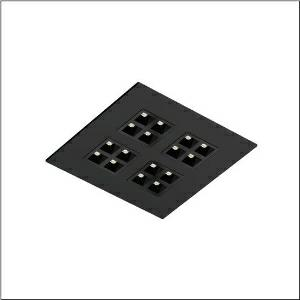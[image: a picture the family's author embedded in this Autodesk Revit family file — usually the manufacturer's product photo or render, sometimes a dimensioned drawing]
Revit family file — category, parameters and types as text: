
# Revit family: silica_31_square_51my6lmu34ba
name_source: partatom
category: Lighting Fixtures
units: mm (PartAtom-declared; Revit-internal decimal feet)

## family parameters
Cut with Voids When Loaded = No
Host = Face
Light Source = No
Part Type = Normal
Room Calculation Point = No
Round Connector Dimension = Use Diameter
Shared = No

## types (1)
- --- (1 x LED, 6250 lm, 39 W, 3000K)
    Apparent Load = 39 VA
    CIE Flux Codes = 82 100 100 100 100
    Color Rendering = 80
    Color Temperature = 3000K
    Default Elevation = 1800 mm
    Description = Silica 31 Square, office luminaire, primary light control with lens, of PMMA, primary anti-glare with reflector, of PC, black, light emission: direct distribution, primary light characteristic: symmetric, installation type: lay-in mounting, LED, rated luminous flux: 4.600lm, luminous efficacy: 166lm/W, light colour: 830, colour temperature: 3000K, control gear: ON/OFF Multilumen, with terminal, 3-pole, mains connection: 220..240V, AC, 50/60Hz, rated input power: 27.7W, luminaire housing, of sheet steel, coated, jet black (RAL 9005), module: M625, length: 620mm, width: 620mm, height: 43mm, protection rating (complete): IP20, insulation class (complete): insulation class II (safety insulation), certification: CE, impact resistance: IK03, permissible operating ambient temperature: -20..+35°C, standard: EN 50419, packaging unit: 1 piece
    Height = 0 mm  [stored 0 ft]
    Lamp = 1 x LED
    Lamp Light Flux = 6250 lm
    Lamp Power = 39 W
    Lamp count = 1
    Length = 620 mm
    Luminous efficacy = 160 lm/W
    Manufacturer = Siteco
    ModVariant = No
    Model = 51MY6LMU34BA
    Mounting Place = Ceiling
    Mounting Type = Recessed
    Number of Poles = 1
    OnlyDefault = Yes
    Power Factor = 1
    Product Name = Silica 31 Square
    Product group = office luminaire | ceiling recessed
    ProductGroupID = 400
    Protection Class = Protection class II
    Protection Degree = IP 20
    RLX_Detail_Level = 1
    RLX_Emergency_Light_Flux = 0 lm
    RLX_Emergency_Type = 0
    RLX_Emergency_Type_DB = No
    RlxData = <blob elided: 36257 chars, md5=d2c4e853>
    Socket = socket
    Standby Power = 0 W
    System Light Flux = 6250 lm
    System Power = 39 W
    Type Comments = factory setting: luminous flux: 100 % | (ON | ON | ON | ON) | 1100 mA
    Type Image = l_1313660.jpg
    URL = http://relux.com
    VarID = @adj_043295
    Voltage = 0 V
    Weight = 0.00 kg
    Width = 620 mm

note: [stored X ft] marks values corroborated as IEEE doubles in the binary element streams (Revit-internal decimal feet)

## geometry (parser evidence)
native form markers: Blend x4, Sweep x10
no freeform markers — native parametric forms only
